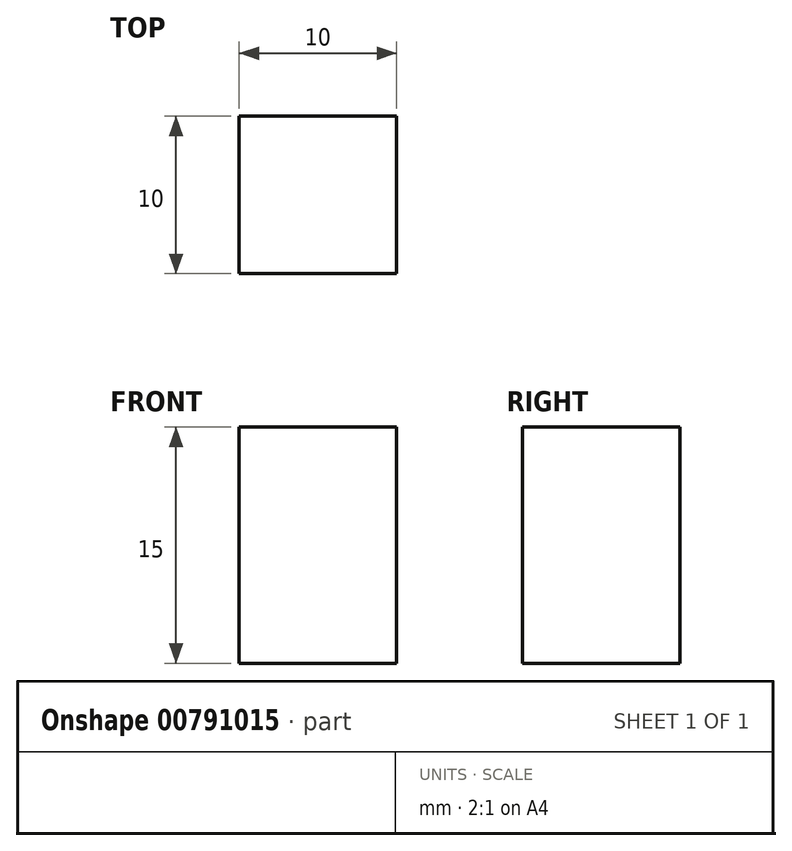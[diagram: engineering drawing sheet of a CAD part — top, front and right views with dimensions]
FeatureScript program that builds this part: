
annotation { "Feature Type Name" : "Feature", "Feature Type Description" : "" }
export const myFeature = defineFeature(function(context is Context, id is Id, definition is map)
    precondition{}
    {
        {
            var Q0;
            Q0=qCreatedBy(makeId("Top.planeOp"),FACE);
            var sketch = newSketch(context, id + "F0", { "sketchPlane" : qUnion([Q0])});
            skLineSegment(sketch, "E0.bottom", {"start": v(-0.51, 6) * mm, "end": v(9.49, 6) * mm});
            skLineSegment(sketch, "E0.top", {"start": v(-0.51, -4) * mm, "end": v(9.49, -4) * mm});
            skLineSegment(sketch, "E0.left", {"start": v(-0.51, 6) * mm, "end": v(-0.51, -4) * mm});
            skLineSegment(sketch, "E0.right", {"start": v(9.49, 6) * mm, "end": v(9.49, -4) * mm});
            skSolve(sketch);
        }
        {
            var Q0;
            Q0 = qSketchRegion(id + "F0", true);
            extrude(context, id + "F1", {"entities" : qUnion([Q0]), "depth" : 15 * mm, "offsetDistance" : 25 * mm});
        }
    });
